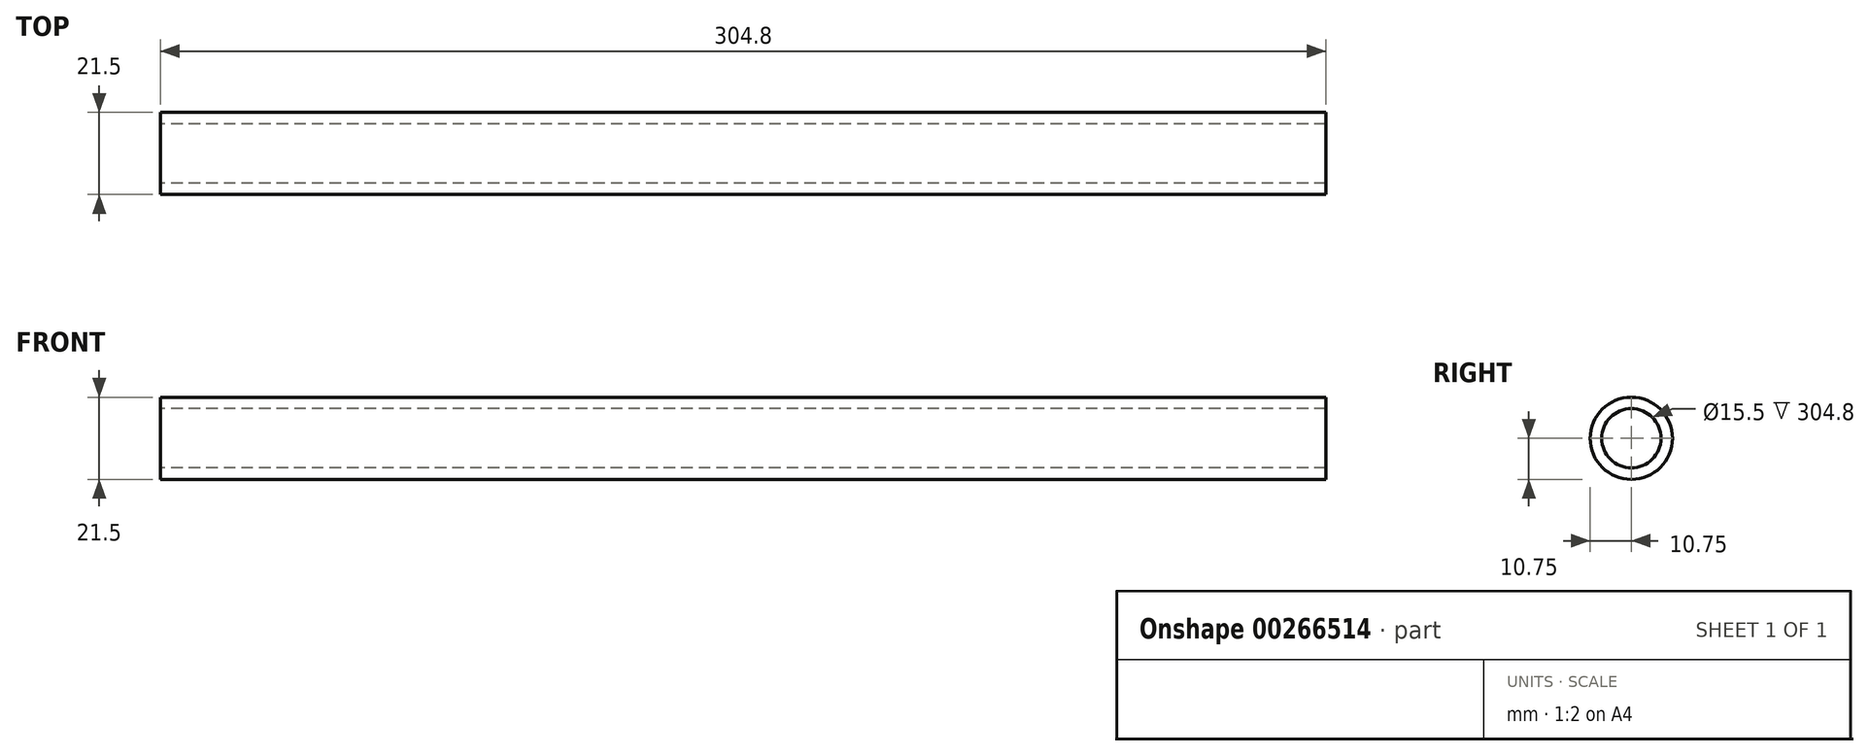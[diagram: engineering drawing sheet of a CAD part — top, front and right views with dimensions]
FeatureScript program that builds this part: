
annotation { "Feature Type Name" : "Feature", "Feature Type Description" : "" }
export const myFeature = defineFeature(function(context is Context, id is Id, definition is map)
    precondition{}
    {
        {
            var Q0;
            Q0=qCreatedBy(makeId("Right.planeOp"),FACE);
            var sketch = newSketch(context, id + "F0", { "sketchPlane" : qUnion([Q0])});
            skCircle(sketch, "E0", {"center": v(0, 0) * mm, "radius": 7.75 * mm});
            skCircle(sketch, "E1", {"center": v(0, 0) * mm, "radius": 10.75 * mm});
            skSolve(sketch);
        }
        {
            var Q0;
            Q0 = qSketchRegion(id + "F0", true);
            extrude(context, id + "F1", {"entities" : qUnion([Q0]), "depth" : 304.8 * mm});
        }
    });
